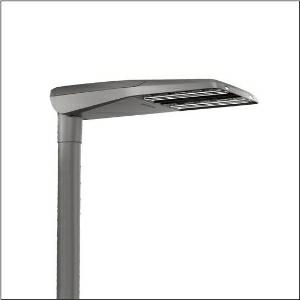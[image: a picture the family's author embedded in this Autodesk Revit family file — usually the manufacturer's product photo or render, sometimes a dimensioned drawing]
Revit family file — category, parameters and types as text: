
# Revit family: streetlight_sl_11_iq_midi___st0_5a_5xc3b41f08le_af5b
name_source: partatom
category: Lighting Fixtures
units: mm (PartAtom-declared; Revit-internal decimal feet)

## family parameters
Cut with Voids When Loaded = No
Host = Face
Light Source = No
Part Type = Normal
Room Calculation Point = No
Round Connector Dimension = Use Diameter
Shared = No

## types (1)
- --- (1 x LED, 9500 lm, 60.4 W, 4000K)
    Apparent Load = 60 VA
    CIE Flux Codes = 43 74 97 100 100
    Color Rendering = 70
    Color Temperature = 4000K
    Default Elevation = 1800 mm
    Description = Streetlight SL 11 iQ midi, mast luminaire, primary light control with 3 zone facetted reflector, of plastic, silver coated, highly specular, primary optical cover: cover, of PMMA, transparent, light distribution: ST0.5a, light emission: direct distribution, primary light characteristic: asymmetric, installation type: post-top, side-entry, LED, High Power LED, rated luminous flux: 9.500lm, luminous efficacy: 157lm/W, light colour: 740, colour temperature: 4000K, control: Street-Remote, optimised constant luminous flux control (CLO 2.0), Desk-Remote (wireless, voltage-free reading and setting of iQ features in the workshop via application-optimized NFC function/RFID function), Light-Fading, Smart-Wire, Night-Set, Lumen-Switch, Temp-Guard, Auto-Match, with cable H07RN-F 5x 1.5mm², mains connection: 220..240V, AC, 50/60Hz, connection cable pre-assembled, cable length: 8,5m, start of lifetime: 60W, end of lifetime: 63W, reduction: 30W, luminaire housing, of diecast aluminium, powder-coated, Siteco® metallic grey (DB 702S), length: 780mm, width: 376mm, height: 118mm, spigot size: 60/76mm (post-top) and 42/60/76mm (side-entry), mast flange for spigot size: 42mm: 5XC10008XM4, 60mm: 5XC10008XM2, 76/60mm: 5XC10108XM1, equipment: standard, protection rating (complete): IP66, insulation class (complete): insulation class II (safety insulation), certification: CE, ENEC, VDE, impact resistance: IK09, permissible operating ambient temperature for outdoor applications: -25..+50°C, standard-compliant lighting for roads and squares, packaging unit: 1 piece

Light Distribution: ST0.5a
    Height = 118 mm
    Lamp = 1 x LED
    Lamp Light Flux = 9500 lm
    Lamp Power = 60.4 W
    Lamp count = 1
    Length = 780 mm
    Luminous efficacy = 157 lm/W
    Manufacturer = Siteco
    ModVariant = No
    Model = 5XC3B41F08LE
    Number of Poles = 1
    OnlyDefault = Yes
    Power Factor = 1
    Product Name = Streetlight SL 11 iQ midi | ST0.5a
    Product group = mast luminaire | pylon top
    ProductGroupID = 6100
    Protection Class = Protection class II
    Protection Degree = IP 66
    RLX_Detail_Level = 1
    RlxData = <blob elided: 74973 chars, md5=2eeb9095>
    Socket = socket
    Standby Power = 0 W
    System Light Flux = 9500 lm
    System Power = 60 W
    Type Comments = factory setting: luminous flux: 100 % | dim-lin: 254 | 520 mA
    Type Image = l_1005960.jpg
    URL = http://relux.com
    VarID = @adj_086897
    Voltage = 0 V
    Weight = 0.00 kg
    Width = 376 mm

## geometry (parser evidence)
native form markers: Blend x4, Sweep x9
no freeform markers — native parametric forms only
